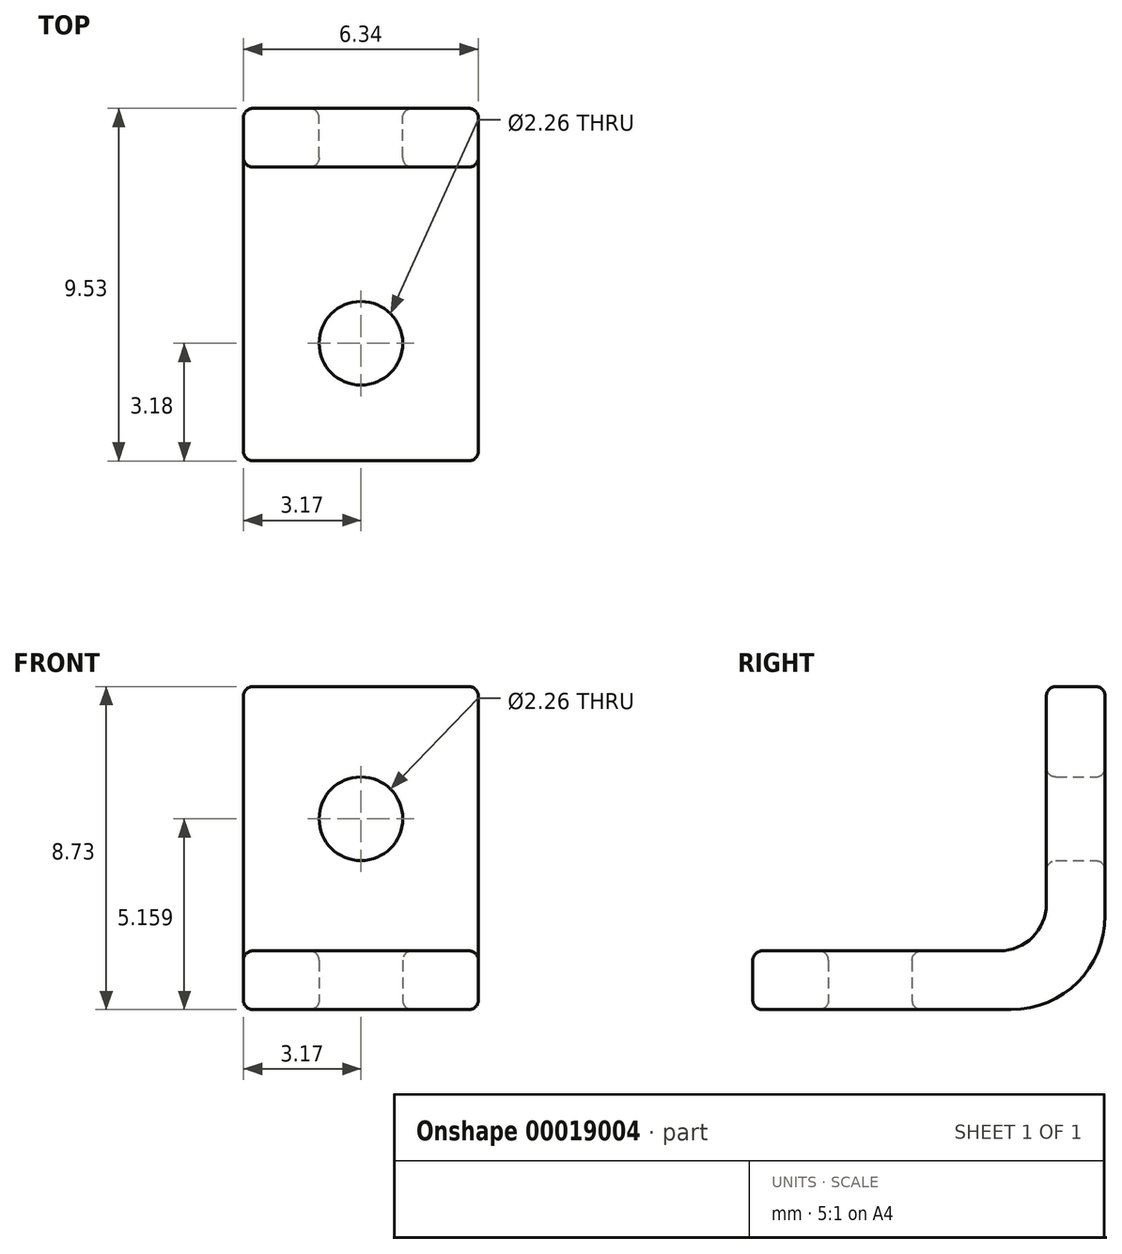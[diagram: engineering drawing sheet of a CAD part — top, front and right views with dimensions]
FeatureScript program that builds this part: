
annotation { "Feature Type Name" : "Feature", "Feature Type Description" : "" }
export const myFeature = defineFeature(function(context is Context, id is Id, definition is map)
    precondition{}
    {
        {
            var Q0;
            Q0=qCreatedBy(makeId("Front.planeOp"),FACE);
            var sketch = newSketch(context, id + "F0", { "sketchPlane" : qUnion([Q0])});
            skLineSegment(sketch, "E0.bottom", {"start": v(-3.18, 8.73) * mm, "end": v(3.18, 8.73) * mm});
            skLineSegment(sketch, "E0.top", {"start": v(-3.18, 0) * mm, "end": v(3.18, 0) * mm});
            skLineSegment(sketch, "E0.left", {"start": v(-3.18, 8.73) * mm, "end": v(-3.18, 0) * mm});
            skLineSegment(sketch, "E0.right", {"start": v(3.17, 8.73) * mm, "end": v(3.17, 0) * mm});
            skLineSegment(sketch, "E1", {"start": v(-3.18, 1.59) * mm, "end": v(3.18, 1.59) * mm});
            skCircle(sketch, "E2", {"center": v(0, 5.16) * mm, "radius": 1.13 * mm});
            skSolve(sketch);
        }
        {
            var Q0;
            Q0=qSketchRegion(id+"F0",true);
            extrude(context, id + "F1", {"entities" : qUnion([Q0]), "depth" : 1.59 * mm});
        }
        {
            var Q0;
            {var subQ2=sQuery(id+"F0.wireOp",EDGE,"E0.top");Q0=makeQuery(id+"F0.imprint","IMPRINT",FACE,{"disambiguationData":[TD([[makeQuery(id+"F0.imprint","IMPRINT",EDGE,{"derivedFrom":subQ2}),1.0]])]});}
            extrude(context, id + "F2", {"entities" : qUnion([Q0]), "operationType" : NewBodyOperationType.ADD, "depth" : 9.52 * mm});
        }
        {
            var Q0;
            {var subQ0=sQuery(id+"F0.wireOp",EDGE,"E0.top");Q0=makeQuery(id+"F2.boolean.opBoolean","MERGE",FACE,{"derivedFrom":[makeQuery(id+"F1.opExtrude","SWEPT_FACE",FACE,{"disambiguationData":[OSD([subQ0])]}),makeQuery(id+"F2.opExtrude","SWEPT_FACE",FACE,{"disambiguationData":[OSD([subQ0])]})]});}
            var sketch = newSketch(context, id + "F3", { "sketchPlane" : qUnion([Q0])});
            skCircle(sketch, "E3", {"center": v(0, 6.35) * mm, "radius": 1.13 * mm});
            skSolve(sketch);
        }
        {
            var Q0;
            Q0=qSketchRegion(id+"F3",true);
            extrude(context, id + "F4", {"entities" : qUnion([Q0]), "operationType" : NewBodyOperationType.REMOVE, "endBound" : BoundingType.UP_TO_NEXT, "oppositeDirection" : true, "depth" : 25.4 * mm});
        }
        {
            var Q0;
            Q0=makeQuery(id+"F1.opExtrude","CAP_EDGE",EDGE,{"disambiguationData":[OSD([sQuery(id+"F0.wireOp",EDGE,"E0.top")])],"isStart":true});
            fillet(context, id + "F5", {"entities" : qUnion([Q0]), "radius" : 2.54 * mm, "tangentPropagation" : true, "allowEdgeOverflow" : false});
        }
        {
            var Q0;
            Q0=makeQuery(id+"F2.boolean.opBoolean","INTERSECT",EDGE,{"derivedFrom":[makeQuery(id+"F1.opExtrude","CAP_FACE",FACE,{"disambiguationData":[OSD([sQuery(id+"F0.wireOp",EDGE,"E0.bottom"),sQuery(id+"F0.wireOp",EDGE,"E0.top"),sQuery(id+"F0.wireOp",EDGE,"E0.left"),sQuery(id+"F0.wireOp",EDGE,"E0.right"),sQuery(id+"F0.wireOp",EDGE,"E2")])],"isStart":false}),makeQuery(id+"F2.opExtrude","SWEPT_FACE",FACE,{"disambiguationData":[OSD([sQuery(id+"F0.wireOp",EDGE,"E1")])]})]});
            fillet(context, id + "F6", {"entities" : qUnion([Q0]), "radius" : 1.27 * mm, "tangentPropagation" : true, "allowEdgeOverflow" : false});
        }
        {
            var Q0;
            {var subQ0=sQuery(id+"F0.wireOp",EDGE,"E0.right");Q0=makeQuery(id+"F2.boolean.opBoolean","MERGE",FACE,{"derivedFrom":[makeQuery(id+"F1.opExtrude","SWEPT_FACE",FACE,{"disambiguationData":[OSD([subQ0])]}),makeQuery(id+"F2.opExtrude","SWEPT_FACE",FACE,{"disambiguationData":[OSD([subQ0])]})]});}
            var Q1;
            {var subQ0=sQuery(id+"F0.wireOp",EDGE,"E0.left");Q1=makeQuery(id+"F2.boolean.opBoolean","MERGE",FACE,{"derivedFrom":[makeQuery(id+"F1.opExtrude","SWEPT_FACE",FACE,{"disambiguationData":[OSD([subQ0])]}),makeQuery(id+"F2.opExtrude","SWEPT_FACE",FACE,{"disambiguationData":[OSD([subQ0])]})]});}
            var Q2;
            Q2=makeQuery(id+"F1.opExtrude","SWEPT_FACE",FACE,{"disambiguationData":[OSD([sQuery(id+"F0.wireOp",EDGE,"E0.bottom")])]});
            var Q3;
            Q3=makeQuery(id+"F5.opFillet","BLEND_FACE",FACE,{"disambiguationData":[OSD([sQuery(id+"F0.wireOp",EDGE,"E0.bottom"),sQuery(id+"F0.wireOp",EDGE,"E0.top"),sQuery(id+"F0.wireOp",EDGE,"E0.left"),sQuery(id+"F0.wireOp",EDGE,"E0.right"),sQuery(id+"F0.wireOp",EDGE,"E1"),sQuery(id+"F0.wireOp",EDGE,"E2")])]});
            var Q4;
            Q4=makeQuery(id+"F2.opExtrude","SWEPT_FACE",FACE,{"disambiguationData":[OSD([sQuery(id+"F0.wireOp",EDGE,"E1")])]});
            var Q5;
            Q5=makeQuery(id+"F2.opExtrude","CAP_EDGE",EDGE,{"disambiguationData":[OSD([sQuery(id+"F0.wireOp",EDGE,"E0.top")])],"isStart":false});
            var Q6;
            Q6=makeQuery(id+"F1.opExtrude","CAP_FACE",FACE,{"disambiguationData":[OSD([sQuery(id+"F0.wireOp",EDGE,"E0.bottom"),sQuery(id+"F0.wireOp",EDGE,"E0.top"),sQuery(id+"F0.wireOp",EDGE,"E0.left"),sQuery(id+"F0.wireOp",EDGE,"E0.right"),sQuery(id+"F0.wireOp",EDGE,"E2")])],"isStart":false});
            var Q7;
            Q7=makeQuery(id+"F1.opExtrude","CAP_FACE",FACE,{"disambiguationData":[OSD([sQuery(id+"F0.wireOp",EDGE,"E0.bottom"),sQuery(id+"F0.wireOp",EDGE,"E0.top"),sQuery(id+"F0.wireOp",EDGE,"E0.left"),sQuery(id+"F0.wireOp",EDGE,"E0.right"),sQuery(id+"F0.wireOp",EDGE,"E2")])],"isStart":true});
            var Q8;
            {var subQ0=sQuery(id+"F0.wireOp",EDGE,"E0.top");Q8=makeQuery(id+"F2.boolean.opBoolean","MERGE",FACE,{"derivedFrom":[makeQuery(id+"F1.opExtrude","SWEPT_FACE",FACE,{"disambiguationData":[OSD([subQ0])]}),makeQuery(id+"F2.opExtrude","SWEPT_FACE",FACE,{"disambiguationData":[OSD([subQ0])]})]});}
            var Q9;
            Q9=makeQuery(id+"F5.opFillet","BLEND_FACE",FACE,{"disambiguationData":[OSD([sQuery(id+"F0.wireOp",EDGE,"E0.top")])]});
            fillet(context, id + "F7", {"entities" : qUnion([Q0, Q1, Q2, Q3, Q4, Q5, Q6, Q7, Q8, Q9]), "radius" : 0.25 * mm, "tangentPropagation" : true, "allowEdgeOverflow" : false});
        }
    });
